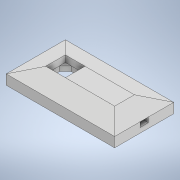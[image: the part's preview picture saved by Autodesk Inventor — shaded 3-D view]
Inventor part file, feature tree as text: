
AUTODESK INVENTOR PART (.ipt)
format: ipt  version: 2020 (Build 240168000, 168)  size: 271,360 bytes
history: native  units: mm
features: sketch x16, extrude x15
ambient origin geometry x8: Origin, YZ Plane, XZ Plane, XY Plane, X Axis, Y Axis, Z Axis, Center Point
bodies: Solid1 (feature_tree)
feature tree (31):
  extrude  "Extrusion1"  Depth=10.0mm
  extrude  "Extrusion2"  Depth=5.0mm
  extrude  "Extrusion3"  Depth=12.0mm
  extrude  "Extrusion4"  Depth=1.0mm
  extrude  "Extrusion5"  Depth=2.0mm TaperAngle=0.0deg
  extrude  "Extrusion6"  Depth=4.0mm
  extrude  "Extrusion7"  Depth=2.0mm
  extrude  "Extrusion8"  Depth=1.0mm TaperAngle=0.0deg
  extrude  "Extrusion9"  Depth=4.0mm
  extrude  "Extrusion10"  Depth=41.75mm TaperAngle=0.0deg
  extrude  "Extrusion11"  Depth=4.0mm
  extrude  "Extrusion12"  Depth=4.0mm TaperAngle=0.0deg
  extrude  "Extrusion13"  Depth=10.0mm
  extrude  "Extrusion14"  Depth=1.5mm TaperAngle=0.0deg
  sketch  "Sketch15"  dims[d41=26.0mm d42=0.0mm d43=3.997397mm]
  extrude  "Extrusion15"  Depth=3.997397mm
  sketch  "Sketch1"  dims[d0=10.0mm d1=10.0mm]
  sketch  "Sketch2"  dims[d2=5.0mm d3=5.0mm]
  sketch  "Sketch3"  dims[d4=12.0mm d5=12.0mm]
  sketch  "Sketch4"  dims[d6=1.0mm d7=1.0mm]
  sketch  "Sketch5"  dims[d8=2.0mm d9=0.0mm d10=11.5mm d11=0.0mm]
  sketch  "Sketch6"  dims[d13=4.0mm d14=4.0mm]
  sketch  "Sketch7"  dims[d15=2.0mm d16=2.0mm]
  sketch  "Sketch8"  dims[d17=23.25mm d18=0.0mm d19=1.0mm d20=0.0mm]
  sketch  "Sketch9"  dims[d21=25.0mm d22=0.0mm d23=4.0mm]
  sketch  "Sketch10"  dims[d24=23.25mm d25=0.0mm d26=41.75mm d27=0.0mm]
  sketch  "Sketch11"  dims[d28=11.625mm d29=0.0mm d30=4.0mm]
  sketch  "Sketch12"  dims[d31=4.0mm d32=105.0mm d33=0.0mm]
  sketch  "Sketch13"  dims[d34=10.0mm d35=0.0mm d36=10.0mm]
  sketch  "Sketch14"  dims[d37=4.25mm d38=0.0mm d39=1.5mm d40=0.0mm]
  sketch  "Sketch16"  dims[d44=3.997397mm d45=17.75mm d46=0.0mm d47=17.75mm d48=0.0mm d49=1.1mm d50=4.75mm d51=0.0mm]
